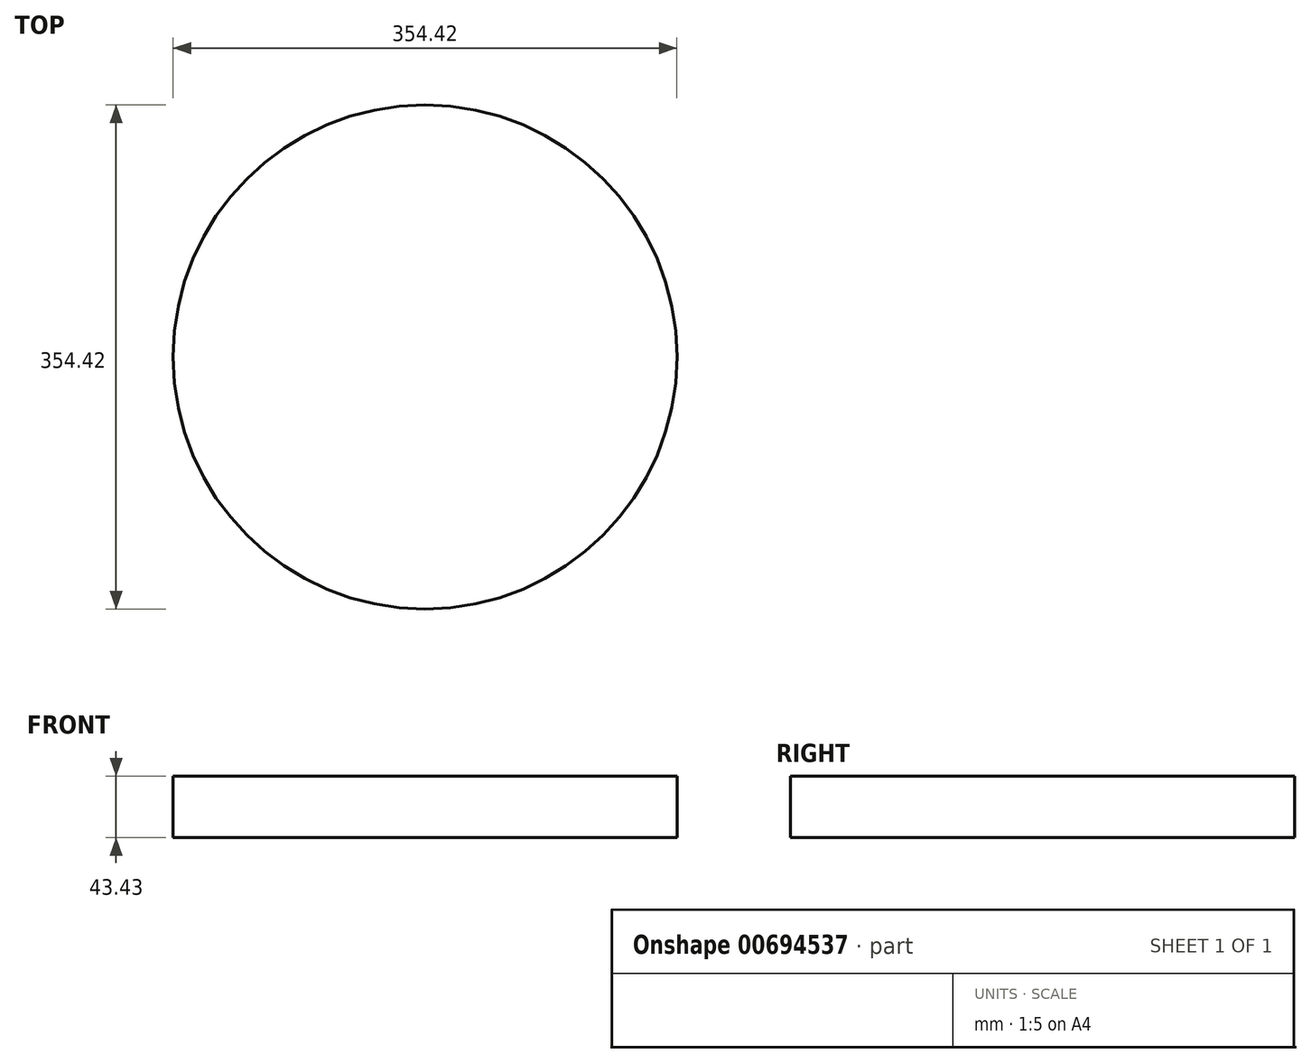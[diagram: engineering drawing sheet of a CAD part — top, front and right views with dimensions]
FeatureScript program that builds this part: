
annotation { "Feature Type Name" : "Feature", "Feature Type Description" : "" }
export const myFeature = defineFeature(function(context is Context, id is Id, definition is map)
    precondition{}
    {
        {
            var Q0;
            Q0=qCreatedBy(makeId("Top.planeOp"),FACE);
            var sketch = newSketch(context, id + "F0", { "sketchPlane" : qUnion([Q0])});
            skCircle(sketch, "E0", {"center": v(0, 0) * mm, "radius": 177.21 * mm});
            skSolve(sketch);
        }
        {
            var Q0;
            Q0 = qSketchRegion(id + "F0", true);
            extrude(context, id + "F1", {"entities" : qUnion([Q0]), "depth" : 43.43 * mm, "offsetDistance" : 25.4 * mm});
        }
    });
